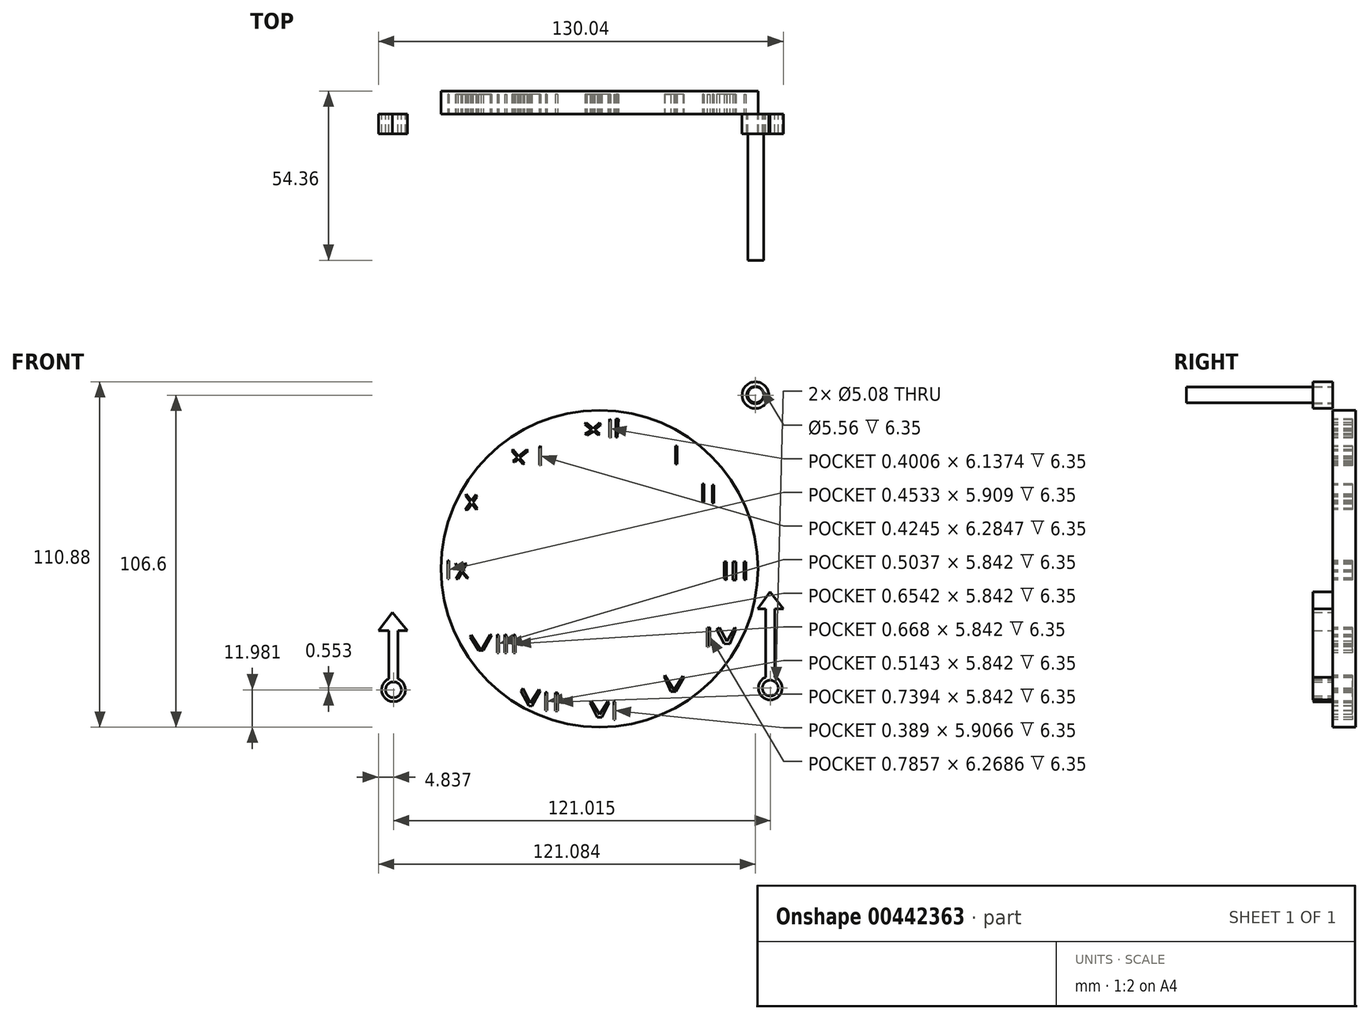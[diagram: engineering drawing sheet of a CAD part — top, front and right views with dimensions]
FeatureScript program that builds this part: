
annotation { "Feature Type Name" : "Feature", "Feature Type Description" : "" }
export const myFeature = defineFeature(function(context is Context, id is Id, definition is map)
    precondition{}
    {
        {
            var Q0;
            Q0=qCreatedBy(makeId("Front.planeOp"),FACE);
            var sketch = newSketch(context, id + "F0", { "sketchPlane" : qUnion([Q0])});
            skLineSegment(sketch, "E0", {"start": v(5.2, 48.06) * mm, "end": v(5.2, 42.22) * mm});
            skLineSegment(sketch, "E1", {"start": v(24.33, 39.4) * mm, "end": v(24.33, 33.55) * mm});
            skLineSegment(sketch, "E2", {"start": v(33.55, 27.23) * mm, "end": v(33.55, 21.39) * mm});
            skLineSegment(sketch, "E3", {"start": v(36.69, 26.86) * mm, "end": v(36.69, 21.02) * mm});
            skLineSegment(sketch, "E4", {"start": v(47.01, 2.15) * mm, "end": v(47.01, -3.69) * mm});
            skLineSegment(sketch, "E5", {"start": v(43.88, 2.15) * mm, "end": v(43.88, -3.69) * mm});
            skLineSegment(sketch, "E6", {"start": v(40.74, 2.15) * mm, "end": v(40.74, -3.69) * mm});
            skLineSegment(sketch, "E7", {"start": v(3.18, 42.22) * mm, "end": v(3.18, 48.06) * mm});
            skLineSegment(sketch, "E8", {"start": v(35.4, -18.86) * mm, "end": v(35.4, -24.7) * mm});
            skLineSegment(sketch, "E9", {"start": v(4.6, -42.58) * mm, "end": v(4.6, -48.42) * mm});
            skLineSegment(sketch, "E10", {"start": v(-14.24, -45.7) * mm, "end": v(-14.24, -39.86) * mm});
            skLineSegment(sketch, "E11", {"start": v(-17.34, -45.55) * mm, "end": v(-17.34, -39.7) * mm});
            skLineSegment(sketch, "E12", {"start": v(-41.21, -21.36) * mm, "end": v(-38.04, -26.27) * mm});
            skLineSegment(sketch, "E13", {"start": v(-38.04, -26.27) * mm, "end": v(-35.16, -21.18) * mm});
            skLineSegment(sketch, "E14", {"start": v(-32.84, -21.18) * mm, "end": v(-32.84, -27.02) * mm});
            skLineSegment(sketch, "E15", {"start": v(-30.51, -21.18) * mm, "end": v(-30.51, -27.02) * mm});
            skLineSegment(sketch, "E16", {"start": v(-27.72, -21.18) * mm, "end": v(-27.72, -27.02) * mm});
            skLineSegment(sketch, "E17", {"start": v(-48.34, 2.62) * mm, "end": v(-48.34, -3.23) * mm});
            skLineSegment(sketch, "E18", {"start": v(-46.02, -3.23) * mm, "end": v(-44.58, -0.7) * mm});
            skLineSegment(sketch, "E19", {"start": v(-46.33, 1.42) * mm, "end": v(-44.58, -0.7) * mm});
            skLineSegment(sketch, "E20", {"start": v(-42.77, 23.97) * mm, "end": v(-41.14, 21.84) * mm});
            skLineSegment(sketch, "E21", {"start": v(-39.79, 23.77) * mm, "end": v(-41.14, 21.84) * mm});
            skLineSegment(sketch, "E22", {"start": v(-27.84, 38.3) * mm, "end": v(-26.03, 36.09) * mm});
            skLineSegment(sketch, "E23", {"start": v(-23.3, 38.3) * mm, "end": v(-26.03, 36.09) * mm});
            skLineSegment(sketch, "E24", {"start": v(-19.28, 39.15) * mm, "end": v(-19.28, 33.3) * mm});
            skCircle(sketch, "E25", {"center": v(0, 0) * mm, "radius": 3.18 * mm});
            skCircle(sketch, "E26", {"center": v(-66.18, -38.9) * mm, "radius": 3.81 * mm});
            skLineSegment(sketch, "E27", {"start": v(-64.7, -38.9) * mm, "end": v(-64.7, -19.85) * mm});
            skLineSegment(sketch, "E28", {"start": v(-67.67, -38.9) * mm, "end": v(-67.67, -19.85) * mm});
            skLineSegment(sketch, "E29", {"start": v(-71.02, -19.85) * mm, "end": v(-61.76, -19.85) * mm});
            skLineSegment(sketch, "E30", {"start": v(-71.02, -19.85) * mm, "end": v(-66.48, -14.05) * mm});
            skLineSegment(sketch, "E31", {"start": v(-61.76, -19.85) * mm, "end": v(-66.48, -14.05) * mm});
            skCircle(sketch, "E32", {"center": v(54.83, -38.35) * mm, "radius": 3.81 * mm});
            skLineSegment(sketch, "E33", {"start": v(54.83, -38.35) * mm, "end": v(56.3, -38.35) * mm});
            skLineSegment(sketch, "E34", {"start": v(54.83, -38.35) * mm, "end": v(53.36, -38.35) * mm});
            skLineSegment(sketch, "E35", {"start": v(56.3, -38.35) * mm, "end": v(56.3, -12.95) * mm});
            skLineSegment(sketch, "E36", {"start": v(53.36, -38.35) * mm, "end": v(53.36, -12.95) * mm});
            skLineSegment(sketch, "E37", {"start": v(50.8, -12.95) * mm, "end": v(59.02, -12.95) * mm});
            skLineSegment(sketch, "E38", {"start": v(50.8, -12.95) * mm, "end": v(54.76, -7.43) * mm});
            skLineSegment(sketch, "E39", {"start": v(54.76, -7.43) * mm, "end": v(59.02, -12.95) * mm});
            skCircle(sketch, "E40", {"center": v(-66.18, -38.9) * mm, "radius": 2.54 * mm});
            skCircle(sketch, "E41", {"center": v(54.83, -38.35) * mm, "radius": 2.54 * mm});
            skLineSegment(sketch, "E42", {"start": v(-48.34, 2.62) * mm, "end": v(-48.8, 2.62) * mm});
            skLineSegment(sketch, "E43", {"start": v(-48.8, 2.62) * mm, "end": v(-48.8, -3.3) * mm});
            skLineSegment(sketch, "E44", {"start": v(-48.8, -3.3) * mm, "end": v(-48.34, -3.23) * mm});
            skLineSegment(sketch, "E45", {"start": v(-46.33, 1.42) * mm, "end": v(-46.18, 1.7) * mm});
            skLineSegment(sketch, "E46", {"start": v(-46.18, 1.7) * mm, "end": v(-44.42, -0.42) * mm});
            skLineSegment(sketch, "E47", {"start": v(-42.22, -3.07) * mm, "end": v(-42.6, -3.07) * mm});
            skLineSegment(sketch, "E48", {"start": v(-43.13, 1.85) * mm, "end": v(-42.78, 1.42) * mm});
            skLineSegment(sketch, "E49", {"start": v(-42.78, 1.42) * mm, "end": v(-44.07, -0.84) * mm});
            skLineSegment(sketch, "E50", {"start": v(-45.43, -3.23) * mm, "end": v(-46.02, -3.23) * mm});
            skLineSegment(sketch, "E51", {"start": v(24.33, 39.4) * mm, "end": v(24.87, 39.4) * mm});
            skLineSegment(sketch, "E52", {"start": v(24.87, 39.4) * mm, "end": v(24.87, 33.55) * mm});
            skLineSegment(sketch, "E53", {"start": v(24.87, 33.55) * mm, "end": v(24.33, 33.55) * mm});
            skLineSegment(sketch, "E54", {"start": v(33.55, 27.23) * mm, "end": v(33.02, 27.23) * mm});
            skLineSegment(sketch, "E55", {"start": v(33.02, 27.23) * mm, "end": v(33.02, 21.42) * mm});
            skLineSegment(sketch, "E56", {"start": v(33.02, 21.42) * mm, "end": v(33.55, 21.39) * mm});
            skLineSegment(sketch, "E57", {"start": v(36.69, 26.86) * mm, "end": v(36.17, 26.86) * mm});
            skLineSegment(sketch, "E58", {"start": v(36.17, 26.86) * mm, "end": v(36.17, 21.16) * mm});
            skLineSegment(sketch, "E59", {"start": v(36.17, 21.16) * mm, "end": v(36.69, 21.02) * mm});
            skLineSegment(sketch, "E60", {"start": v(40.74, -3.69) * mm, "end": v(40.07, -3.3) * mm});
            skLineSegment(sketch, "E61", {"start": v(40.07, -3.3) * mm, "end": v(40.07, 2.15) * mm});
            skLineSegment(sketch, "E62", {"start": v(40.07, 2.15) * mm, "end": v(40.74, 2.15) * mm});
            skLineSegment(sketch, "E63", {"start": v(43.88, -3.69) * mm, "end": v(42.75, -3.69) * mm});
            skLineSegment(sketch, "E64", {"start": v(42.75, -3.69) * mm, "end": v(42.75, 2.15) * mm});
            skLineSegment(sketch, "E65", {"start": v(42.75, 2.15) * mm, "end": v(43.88, 2.15) * mm});
            skLineSegment(sketch, "E66", {"start": v(47.01, -3.69) * mm, "end": v(46.34, -3.3) * mm});
            skLineSegment(sketch, "E67", {"start": v(46.34, -3.3) * mm, "end": v(46.34, 2.15) * mm});
            skLineSegment(sketch, "E68", {"start": v(46.34, 2.15) * mm, "end": v(47.01, 2.15) * mm});
            skLineSegment(sketch, "E69", {"start": v(35.4, -24.7) * mm, "end": v(34.61, -25.13) * mm});
            skLineSegment(sketch, "E70", {"start": v(34.61, -25.13) * mm, "end": v(34.61, -19) * mm});
            skLineSegment(sketch, "E71", {"start": v(34.61, -19) * mm, "end": v(35.4, -18.86) * mm});
            skLineSegment(sketch, "E72", {"start": v(38.49, -18.86) * mm, "end": v(37.65, -19.56) * mm});
            skLineSegment(sketch, "E73", {"start": v(43.45, -18.86) * mm, "end": v(43.88, -19.37) * mm});
            skLineSegment(sketch, "E74", {"start": v(21.02, -34.3) * mm, "end": v(20.8, -34.77) * mm});
            skLineSegment(sketch, "E75", {"start": v(26.83, -34.56) * mm, "end": v(27.06, -35.02) * mm});
            skLineSegment(sketch, "E76", {"start": v(27.06, -35.02) * mm, "end": v(24.49, -39.52) * mm});
            skLineSegment(sketch, "E77", {"start": v(4.6, -42.58) * mm, "end": v(5, -42.76) * mm});
            skLineSegment(sketch, "E78", {"start": v(5, -42.76) * mm, "end": v(5, -48.48) * mm});
            skLineSegment(sketch, "E79", {"start": v(5, -48.48) * mm, "end": v(4.6, -48.42) * mm});
            skLineSegment(sketch, "E80", {"start": v(2.72, -42.58) * mm, "end": v(3, -43.1) * mm});
            skLineSegment(sketch, "E81", {"start": v(3, -43.1) * mm, "end": v(0.82, -47.75) * mm});
            skLineSegment(sketch, "E82", {"start": v(-2.66, -42.55) * mm, "end": v(-3.06, -43.17) * mm});
            skLineSegment(sketch, "E83", {"start": v(-3.06, -43.17) * mm, "end": v(-0.72, -47.75) * mm});
            skLineSegment(sketch, "E84", {"start": v(20.8, -34.77) * mm, "end": v(22.9, -39.43) * mm});
            skLineSegment(sketch, "E85", {"start": v(43.88, -19.37) * mm, "end": v(41.8, -24.25) * mm});
            skLineSegment(sketch, "E86", {"start": v(-19.36, -38.88) * mm, "end": v(-19.04, -39.3) * mm});
            skLineSegment(sketch, "E87", {"start": v(-19.04, -39.3) * mm, "end": v(-21.66, -44.12) * mm});
            skLineSegment(sketch, "E88", {"start": v(-24.67, -38.4) * mm, "end": v(-25.2, -39.38) * mm});
            skLineSegment(sketch, "E89", {"start": v(-25.2, -39.38) * mm, "end": v(-22.68, -44.03) * mm});
            skLineSegment(sketch, "E90", {"start": v(-17.34, -39.7) * mm, "end": v(-16.82, -39.7) * mm});
            skLineSegment(sketch, "E91", {"start": v(-16.82, -39.7) * mm, "end": v(-16.82, -45.5) * mm});
            skLineSegment(sketch, "E92", {"start": v(-16.82, -45.5) * mm, "end": v(-17.34, -45.55) * mm});
            skLineSegment(sketch, "E93", {"start": v(-14.24, -39.86) * mm, "end": v(-13.5, -39.86) * mm});
            skLineSegment(sketch, "E94", {"start": v(-13.5, -39.86) * mm, "end": v(-13.5, -45.7) * mm});
            skLineSegment(sketch, "E95", {"start": v(-13.5, -45.7) * mm, "end": v(-14.24, -45.7) * mm});
            skLineSegment(sketch, "E96", {"start": v(-35.16, -21.18) * mm, "end": v(-34.69, -21.44) * mm});
            skLineSegment(sketch, "E97", {"start": v(-34.69, -21.44) * mm, "end": v(-37.31, -26.28) * mm});
            skLineSegment(sketch, "E98", {"start": v(-41.21, -21.36) * mm, "end": v(-41.53, -21.94) * mm});
            skLineSegment(sketch, "E99", {"start": v(-41.53, -21.94) * mm, "end": v(-38.87, -26.27) * mm});
            skLineSegment(sketch, "E100", {"start": v(-32.84, -21.18) * mm, "end": v(-32.34, -21.46) * mm});
            skLineSegment(sketch, "E101", {"start": v(-32.34, -21.46) * mm, "end": v(-32.34, -27.02) * mm});
            skLineSegment(sketch, "E102", {"start": v(-32.34, -27.02) * mm, "end": v(-32.84, -27.02) * mm});
            skLineSegment(sketch, "E103", {"start": v(-30.51, -21.18) * mm, "end": v(-29.86, -21.54) * mm});
            skLineSegment(sketch, "E104", {"start": v(-29.86, -21.54) * mm, "end": v(-29.86, -27.02) * mm});
            skLineSegment(sketch, "E105", {"start": v(-29.86, -27.02) * mm, "end": v(-30.51, -27.02) * mm});
            skLineSegment(sketch, "E106", {"start": v(-27.72, -21.18) * mm, "end": v(-27.06, -21.55) * mm});
            skLineSegment(sketch, "E107", {"start": v(-27.06, -21.55) * mm, "end": v(-27.06, -27.02) * mm});
            skLineSegment(sketch, "E108", {"start": v(-27.06, -27.02) * mm, "end": v(-27.72, -27.02) * mm});
            skLineSegment(sketch, "E109", {"start": v(-42.77, 23.97) * mm, "end": v(-43.07, 23.4) * mm});
            skLineSegment(sketch, "E110", {"start": v(-43.07, 23.4) * mm, "end": v(-41.5, 21.34) * mm});
            skLineSegment(sketch, "E111", {"start": v(-39.65, 18.94) * mm, "end": v(-39.22, 19.33) * mm});
            skLineSegment(sketch, "E112", {"start": v(-39.79, 23.77) * mm, "end": v(-39.4, 23.07) * mm});
            skLineSegment(sketch, "E113", {"start": v(-39.4, 23.07) * mm, "end": v(-40.69, 21.24) * mm});
            skLineSegment(sketch, "E114", {"start": v(-42.3, 18.92) * mm, "end": v(-43.14, 18.99) * mm});
            skLineSegment(sketch, "E115", {"start": v(-27.84, 38.3) * mm, "end": v(-28.16, 37.71) * mm});
            skLineSegment(sketch, "E116", {"start": v(-28.16, 37.71) * mm, "end": v(-26.47, 35.74) * mm});
            skLineSegment(sketch, "E117", {"start": v(-24.62, 33.58) * mm, "end": v(-24.15, 33.77) * mm});
            skLineSegment(sketch, "E118", {"start": v(-23.3, 38.3) * mm, "end": v(-23.03, 37.8) * mm});
            skLineSegment(sketch, "E119", {"start": v(-23.03, 37.8) * mm, "end": v(-25.63, 35.59) * mm});
            skLineSegment(sketch, "E120", {"start": v(-27.22, 34.22) * mm, "end": v(-27.84, 34.62) * mm});
            skLineSegment(sketch, "E121", {"start": v(-19.28, 39.15) * mm, "end": v(-18.85, 39.38) * mm});
            skLineSegment(sketch, "E122", {"start": v(-18.85, 39.38) * mm, "end": v(-18.85, 33.1) * mm});
            skLineSegment(sketch, "E123", {"start": v(-18.85, 33.1) * mm, "end": v(-19.28, 33.3) * mm});
            skLineSegment(sketch, "E124", {"start": v(-4.35, 46.85) * mm, "end": v(-4.64, 46.31) * mm});
            skLineSegment(sketch, "E125", {"start": v(-0.37, 42.83) * mm, "end": v(0, 43.3) * mm});
            skLineSegment(sketch, "E126", {"start": v(0, 46.85) * mm, "end": v(0.42, 46.07) * mm});
            skLineSegment(sketch, "E127", {"start": v(-4.09, 42.83) * mm, "end": v(-4.64, 43.3) * mm});
            skLineSegment(sketch, "E128", {"start": v(3.17, 48.06) * mm, "end": v(3.58, 47.84) * mm});
            skLineSegment(sketch, "E129", {"start": v(3.58, 47.84) * mm, "end": v(3.58, 41.92) * mm});
            skLineSegment(sketch, "E130", {"start": v(3.58, 41.92) * mm, "end": v(3.18, 42.22) * mm});
            skLineSegment(sketch, "E131", {"start": v(5.2, 48.06) * mm, "end": v(6.05, 48.06) * mm});
            skLineSegment(sketch, "E132", {"start": v(6.05, 48.06) * mm, "end": v(5.7, 42.22) * mm});
            skLineSegment(sketch, "E133", {"start": v(5.7, 42.22) * mm, "end": v(5.2, 42.22) * mm});
            skLineSegment(sketch, "E134", {"start": v(39.99, -24.11) * mm, "end": v(37.65, -19.56) * mm});
            skLineSegment(sketch, "E135", {"start": v(0.42, 46.07) * mm, "end": v(-1.45, 44.56) * mm});
            skLineSegment(sketch, "E136", {"start": v(-1.45, 44.56) * mm, "end": v(0, 43.3) * mm});
            skLineSegment(sketch, "E137", {"start": v(-0.37, 42.83) * mm, "end": v(-1.95, 44.07) * mm});
            skLineSegment(sketch, "E138", {"start": v(-1.95, 44.07) * mm, "end": v(-4.09, 42.83) * mm});
            skLineSegment(sketch, "E139", {"start": v(-4.64, 43.3) * mm, "end": v(-2.48, 44.55) * mm});
            skLineSegment(sketch, "E140", {"start": v(-2.48, 44.55) * mm, "end": v(-4.64, 46.31) * mm});
            skLineSegment(sketch, "E141", {"start": v(-4.35, 46.85) * mm, "end": v(-2.02, 44.93) * mm});
            skLineSegment(sketch, "E142", {"start": v(-2.02, 44.93) * mm, "end": v(0, 46.85) * mm});
            skLineSegment(sketch, "E143.trimOffspring", {"start": v(-25.63, 35.59) * mm, "end": v(-24.15, 33.77) * mm});
            skLineSegment(sketch, "E144.trimOffspring", {"start": v(-26.47, 35.74) * mm, "end": v(-27.84, 34.62) * mm});
            skLineSegment(sketch, "E145.trimOffspring", {"start": v(-26.03, 35.23) * mm, "end": v(-24.62, 33.58) * mm});
            skLineSegment(sketch, "E146.trimOffspring", {"start": v(-26.03, 35.23) * mm, "end": v(-27.22, 34.22) * mm});
            skLineSegment(sketch, "E147.trimOffspring", {"start": v(-41.5, 21.34) * mm, "end": v(-43.14, 18.99) * mm});
            skLineSegment(sketch, "E148.trimOffspring", {"start": v(-41.03, 20.74) * mm, "end": v(-39.65, 18.94) * mm});
            skLineSegment(sketch, "E149.trimOffspring", {"start": v(-41.03, 20.74) * mm, "end": v(-42.3, 18.92) * mm});
            skLineSegment(sketch, "E150.trimOffspring", {"start": v(-40.69, 21.24) * mm, "end": v(-39.22, 19.33) * mm});
            skLineSegment(sketch, "E151", {"start": v(41.8, -24.25) * mm, "end": v(39.99, -24.11) * mm});
            skLineSegment(sketch, "E152", {"start": v(24.49, -39.52) * mm, "end": v(22.9, -39.43) * mm});
            skLineSegment(sketch, "E153", {"start": v(0.82, -47.75) * mm, "end": v(-0.72, -47.75) * mm});
            skLineSegment(sketch, "E154", {"start": v(-19.36, -38.88) * mm, "end": v(-22.16, -43.08) * mm});
            skLineSegment(sketch, "E155", {"start": v(-37.31, -26.28) * mm, "end": v(-38.87, -26.27) * mm});
            skLineSegment(sketch, "E156.trimOffspring", {"start": v(-44.23, -1.12) * mm, "end": v(-45.43, -3.23) * mm});
            skLineSegment(sketch, "E157.trimOffspring", {"start": v(-44.23, -1.12) * mm, "end": v(-42.6, -3.07) * mm});
            skLineSegment(sketch, "E158.trimOffspring", {"start": v(-44.42, -0.42) * mm, "end": v(-43.13, 1.85) * mm});
            skLineSegment(sketch, "E159.trimOffspring", {"start": v(-44.07, -0.84) * mm, "end": v(-42.22, -3.07) * mm});
            skLineSegment(sketch, "E160", {"start": v(-21.66, -44.12) * mm, "end": v(-22.68, -44.03) * mm});
            skLineSegment(sketch, "E161", {"start": v(-24.67, -38.4) * mm, "end": v(-22.16, -43.08) * mm});
            skLineSegment(sketch, "E162", {"start": v(26.83, -34.56) * mm, "end": v(23.9, -38.98) * mm});
            skLineSegment(sketch, "E163", {"start": v(23.9, -38.98) * mm, "end": v(21.02, -34.3) * mm});
            skLineSegment(sketch, "E164", {"start": v(2.72, -42.58) * mm, "end": v(0, -46.85) * mm});
            skLineSegment(sketch, "E165", {"start": v(0, -46.85) * mm, "end": v(-2.66, -42.55) * mm});
            skLineSegment(sketch, "E166", {"start": v(43.45, -18.86) * mm, "end": v(40.91, -23.33) * mm});
            skLineSegment(sketch, "E167", {"start": v(40.91, -23.33) * mm, "end": v(38.49, -18.86) * mm});
            skSolve(sketch);
        }
        {
            var Q0;
            {var subQ0=sQuery(id+"F0.wireOp",EDGE,"E30");Q0=makeQuery(id+"F0.imprint","IMPRINT",FACE,{"disambiguationData":[TD([[makeQuery(id+"F0.imprint","IMPRINT",EDGE,{"derivedFrom":subQ0}),-1.0]])]});}
            var Q1;
            {var subQ0=sQuery(id+"F0.wireOp",EDGE,"E27");var subQ1=sQuery(id+"F0.wireOp",EDGE,"E26");var subQ2=makeQuery(id+"F0.imprint","INTERSECT",VERTEX,{"derivedFrom":[subQ1,subQ0]});Q1=makeQuery(id+"F0.imprint","IMPRINT",FACE,{"disambiguationData":[TD([[makeQuery(id+"F0.imprint","IMPRINT",EDGE,{"disambiguationData":[TD([[subQ2,-1.0]])],"derivedFrom":subQ1}),-1.0]])]});}
            var Q2;
            {var subQ0=sQuery(id+"F0.wireOp",EDGE,"E27");var subQ1=sQuery(id+"F0.wireOp",EDGE,"E26");var subQ2=makeQuery(id+"F0.imprint","INTERSECT",VERTEX,{"derivedFrom":[subQ1,subQ0]});Q2=makeQuery(id+"F0.imprint","IMPRINT",FACE,{"disambiguationData":[TD([[makeQuery(id+"F0.imprint","IMPRINT",EDGE,{"disambiguationData":[TD([[subQ2,1.0]])],"derivedFrom":subQ1}),1.0]])]});}
            var Q3;
            {var subQ0=sQuery(id+"F0.wireOp",EDGE,"E27");var subQ1=sQuery(id+"F0.wireOp",EDGE,"E26");var subQ2=makeQuery(id+"F0.imprint","INTERSECT",VERTEX,{"derivedFrom":[subQ1,subQ0]});Q3=makeQuery(id+"F0.imprint","IMPRINT",FACE,{"disambiguationData":[TD([[makeQuery(id+"F0.imprint","IMPRINT",EDGE,{"disambiguationData":[TD([[subQ2,-1.0]])],"derivedFrom":subQ1}),1.0]])]});}
            var Q4;
            {var subQ0=sQuery(id+"F0.wireOp",EDGE,"E38");Q4=makeQuery(id+"F0.imprint","IMPRINT",FACE,{"disambiguationData":[TD([[makeQuery(id+"F0.imprint","IMPRINT",EDGE,{"derivedFrom":subQ0}),-1.0]])]});}
            var Q5;
            {var subQ0=sQuery(id+"F0.wireOp",EDGE,"E35");var subQ1=sQuery(id+"F0.wireOp",EDGE,"E32");var subQ2=makeQuery(id+"F0.imprint","INTERSECT",VERTEX,{"derivedFrom":[subQ1,subQ0]});Q5=makeQuery(id+"F0.imprint","IMPRINT",FACE,{"disambiguationData":[TD([[makeQuery(id+"F0.imprint","IMPRINT",EDGE,{"disambiguationData":[TD([[subQ2,-1.0]])],"derivedFrom":subQ1}),-1.0]])]});}
            var Q6;
            {var subQ0=sQuery(id+"F0.wireOp",EDGE,"E35");var subQ1=sQuery(id+"F0.wireOp",EDGE,"E32");var subQ2=makeQuery(id+"F0.imprint","INTERSECT",VERTEX,{"derivedFrom":[subQ1,subQ0]});Q6=makeQuery(id+"F0.imprint","IMPRINT",FACE,{"disambiguationData":[TD([[makeQuery(id+"F0.imprint","IMPRINT",EDGE,{"disambiguationData":[TD([[subQ2,1.0]])],"derivedFrom":subQ1}),1.0]])]});}
            var Q7;
            {var subQ0=sQuery(id+"F0.wireOp",EDGE,"E35");var subQ1=sQuery(id+"F0.wireOp",EDGE,"E32");var subQ2=makeQuery(id+"F0.imprint","INTERSECT",VERTEX,{"derivedFrom":[subQ1,subQ0]});Q7=makeQuery(id+"F0.imprint","IMPRINT",FACE,{"disambiguationData":[TD([[makeQuery(id+"F0.imprint","IMPRINT",EDGE,{"disambiguationData":[TD([[subQ2,-1.0]])],"derivedFrom":subQ1}),1.0]])]});}
            extrude(context, id + "F1", {"entities" : qUnion([Q0, Q1, Q2, Q3, Q4, Q5, Q6, Q7]), "depth" : 6.35 * mm});
        }
        {
            var Q0;
            Q0=qCreatedBy(makeId("Front.planeOp"),FACE);
            var sketch = newSketch(context, id + "F2", { "sketchPlane" : qUnion([Q0])});
            skCircle(sketch, "E168", {"center": v(0, 0) * mm, "radius": 50.88 * mm});
            skSolve(sketch);
        }
        {
            var Q0;
            Q0=makeQuery(id+"F2.imprint","IMPRINT",FACE,{"disambiguationData":[TD([[makeQuery(id+"F2.imprint","IMPRINT",EDGE,{"derivedFrom":sQuery(id+"F2.wireOp",EDGE,"E168")}),1.0]])]});
            extrude(context, id + "F3", {"entities" : qUnion([Q0]), "oppositeDirection" : true, "depth" : 7.37 * mm});
        }
        {
            var Q0;
            Q0=makeQuery(id+"F0.imprint","IMPRINT",FACE,{"disambiguationData":[TD([[makeQuery(id+"F0.imprint","IMPRINT",EDGE,{"derivedFrom":sQuery(id+"F0.wireOp",EDGE,"E18")}),-1.0]])]});
            var Q1;
            Q1=makeQuery(id+"F0.imprint","IMPRINT",FACE,{"disambiguationData":[TD([[makeQuery(id+"F0.imprint","IMPRINT",EDGE,{"derivedFrom":sQuery(id+"F0.wireOp",EDGE,"E17")}),-1.0]])]});
            var Q2;
            Q2=makeQuery(id+"F0.imprint","IMPRINT",FACE,{"disambiguationData":[TD([[makeQuery(id+"F0.imprint","IMPRINT",EDGE,{"derivedFrom":sQuery(id+"F0.wireOp",EDGE,"E20")}),-1.0]])]});
            var Q3;
            Q3=makeQuery(id+"F0.imprint","IMPRINT",FACE,{"disambiguationData":[TD([[makeQuery(id+"F0.imprint","IMPRINT",EDGE,{"derivedFrom":sQuery(id+"F0.wireOp",EDGE,"E22")}),-1.0]])]});
            var Q4;
            Q4=makeQuery(id+"F0.imprint","IMPRINT",FACE,{"disambiguationData":[TD([[makeQuery(id+"F0.imprint","IMPRINT",EDGE,{"derivedFrom":sQuery(id+"F0.wireOp",EDGE,"E24")}),1.0]])]});
            var Q5;
            Q5=makeQuery(id+"F0.imprint","IMPRINT",FACE,{"disambiguationData":[TD([[makeQuery(id+"F0.imprint","IMPRINT",EDGE,{"derivedFrom":sQuery(id+"F0.wireOp",EDGE,"E12")}),-1.0]])]});
            var Q6;
            Q6=makeQuery(id+"F0.imprint","IMPRINT",FACE,{"disambiguationData":[TD([[makeQuery(id+"F0.imprint","IMPRINT",EDGE,{"derivedFrom":sQuery(id+"F0.wireOp",EDGE,"E14")}),1.0]])]});
            var Q7;
            Q7=makeQuery(id+"F0.imprint","IMPRINT",FACE,{"disambiguationData":[TD([[makeQuery(id+"F0.imprint","IMPRINT",EDGE,{"derivedFrom":sQuery(id+"F0.wireOp",EDGE,"E15")}),1.0]])]});
            var Q8;
            Q8=makeQuery(id+"F0.imprint","IMPRINT",FACE,{"disambiguationData":[TD([[makeQuery(id+"F0.imprint","IMPRINT",EDGE,{"derivedFrom":sQuery(id+"F0.wireOp",EDGE,"E16")}),1.0]])]});
            var Q9;
            Q9=makeQuery(id+"F0.imprint","IMPRINT",FACE,{"disambiguationData":[TD([[makeQuery(id+"F0.imprint","IMPRINT",EDGE,{"derivedFrom":sQuery(id+"F0.wireOp",EDGE,"E86")}),-1.0]])]});
            var Q10;
            Q10=makeQuery(id+"F0.imprint","IMPRINT",FACE,{"disambiguationData":[TD([[makeQuery(id+"F0.imprint","IMPRINT",EDGE,{"derivedFrom":sQuery(id+"F0.wireOp",EDGE,"E11")}),-1.0]])]});
            var Q11;
            Q11=makeQuery(id+"F0.imprint","IMPRINT",FACE,{"disambiguationData":[TD([[makeQuery(id+"F0.imprint","IMPRINT",EDGE,{"derivedFrom":sQuery(id+"F0.wireOp",EDGE,"E10")}),-1.0]])]});
            var Q12;
            Q12=makeQuery(id+"F0.imprint","IMPRINT",FACE,{"disambiguationData":[TD([[makeQuery(id+"F0.imprint","IMPRINT",EDGE,{"derivedFrom":sQuery(id+"F0.wireOp",EDGE,"E80")}),-1.0]])]});
            var Q13;
            Q13=makeQuery(id+"F0.imprint","IMPRINT",FACE,{"disambiguationData":[TD([[makeQuery(id+"F0.imprint","IMPRINT",EDGE,{"derivedFrom":sQuery(id+"F0.wireOp",EDGE,"E9")}),1.0]])]});
            var Q14;
            Q14=makeQuery(id+"F0.imprint","IMPRINT",FACE,{"disambiguationData":[TD([[makeQuery(id+"F0.imprint","IMPRINT",EDGE,{"derivedFrom":sQuery(id+"F0.wireOp",EDGE,"E74")}),1.0]])]});
            var Q15;
            Q15=makeQuery(id+"F0.imprint","IMPRINT",FACE,{"disambiguationData":[TD([[makeQuery(id+"F0.imprint","IMPRINT",EDGE,{"derivedFrom":sQuery(id+"F0.wireOp",EDGE,"E8")}),-1.0]])]});
            var Q16;
            Q16=makeQuery(id+"F0.imprint","IMPRINT",FACE,{"disambiguationData":[TD([[makeQuery(id+"F0.imprint","IMPRINT",EDGE,{"derivedFrom":sQuery(id+"F0.wireOp",EDGE,"E72")}),1.0]])]});
            var Q17;
            Q17=makeQuery(id+"F0.imprint","IMPRINT",FACE,{"disambiguationData":[TD([[makeQuery(id+"F0.imprint","IMPRINT",EDGE,{"derivedFrom":sQuery(id+"F0.wireOp",EDGE,"E6")}),-1.0]])]});
            var Q18;
            Q18=makeQuery(id+"F0.imprint","IMPRINT",FACE,{"disambiguationData":[TD([[makeQuery(id+"F0.imprint","IMPRINT",EDGE,{"derivedFrom":sQuery(id+"F0.wireOp",EDGE,"E5")}),-1.0]])]});
            var Q19;
            Q19=makeQuery(id+"F0.imprint","IMPRINT",FACE,{"disambiguationData":[TD([[makeQuery(id+"F0.imprint","IMPRINT",EDGE,{"derivedFrom":sQuery(id+"F0.wireOp",EDGE,"E4")}),-1.0]])]});
            var Q20;
            Q20=makeQuery(id+"F0.imprint","IMPRINT",FACE,{"disambiguationData":[TD([[makeQuery(id+"F0.imprint","IMPRINT",EDGE,{"derivedFrom":sQuery(id+"F0.wireOp",EDGE,"E1")}),1.0]])]});
            var Q21;
            Q21=makeQuery(id+"F0.imprint","IMPRINT",FACE,{"disambiguationData":[TD([[makeQuery(id+"F0.imprint","IMPRINT",EDGE,{"derivedFrom":sQuery(id+"F0.wireOp",EDGE,"E2")}),-1.0]])]});
            var Q22;
            Q22=makeQuery(id+"F0.imprint","IMPRINT",FACE,{"disambiguationData":[TD([[makeQuery(id+"F0.imprint","IMPRINT",EDGE,{"derivedFrom":sQuery(id+"F0.wireOp",EDGE,"E3")}),-1.0]])]});
            var Q23;
            Q23=makeQuery(id+"F0.imprint","IMPRINT",FACE,{"disambiguationData":[TD([[makeQuery(id+"F0.imprint","IMPRINT",EDGE,{"derivedFrom":sQuery(id+"F0.wireOp",EDGE,"E7")}),-1.0]])]});
            var Q24;
            Q24=makeQuery(id+"F0.imprint","IMPRINT",FACE,{"disambiguationData":[TD([[makeQuery(id+"F0.imprint","IMPRINT",EDGE,{"derivedFrom":sQuery(id+"F0.wireOp",EDGE,"E0")}),1.0]])]});
            var Q25;
            Q25=makeQuery(id+"F0.imprint","IMPRINT",FACE,{"disambiguationData":[TD([[makeQuery(id+"F0.imprint","IMPRINT",EDGE,{"derivedFrom":sQuery(id+"F0.wireOp",EDGE,"E124")}),1.0]])]});
            extrude(context, id + "F4", {"entities" : qUnion([Q0, Q1, Q2, Q3, Q4, Q5, Q6, Q7, Q8, Q9, Q10, Q11, Q12, Q13, Q14, Q15, Q16, Q17, Q18, Q19, Q20, Q21, Q22, Q23, Q24, Q25]), "operationType" : NewBodyOperationType.REMOVE, "oppositeDirection" : true, "depth" : 6.35 * mm});
        }
        {
            var Q0;
            Q0=makeQuery(id+"F0.imprint","IMPRINT",FACE,{"disambiguationData":[TD([[makeQuery(id+"F0.imprint","IMPRINT",EDGE,{"derivedFrom":sQuery(id+"F0.wireOp",EDGE,"E25")}),1.0]])]});
            var sketch = newSketch(context, id + "F5", { "sketchPlane" : qUnion([Q0])});
            skCircle(sketch, "E169", {"center": v(0, 0) * mm, "radius": 3.1 * mm});
            skSolve(sketch);
        }
        {
            var Q0;
            Q0=makeQuery(id+"F0.imprint","IMPRINT",FACE,{"disambiguationData":[TD([[makeQuery(id+"F0.imprint","IMPRINT",EDGE,{"derivedFrom":sQuery(id+"F0.wireOp",EDGE,"E25")}),1.0]])]});
            var Q1;
            Q1=sQuery(id+"F5.wireOp",EDGE,"E169");
            extrude(context, id + "F6", {"entities" : qUnion([Q0]), "operationType" : NewBodyOperationType.REMOVE, "surfaceEntities" : qUnion([Q1]), "depth" : 41.4 * mm});
        }
        {
            var Q0;
            Q0=qCreatedBy(makeId("Front.planeOp"),FACE);
            var sketch = newSketch(context, id + "F7", { "sketchPlane" : qUnion([Q0])});
            skCircle(sketch, "E170", {"center": v(50.14, 55.8) * mm, "radius": 2.54 * mm});
            skSolve(sketch);
        }
        {
            var Q0;
            Q0=makeQuery(id+"F7.imprint","IMPRINT",FACE,{"disambiguationData":[TD([[makeQuery(id+"F7.imprint","IMPRINT",EDGE,{"derivedFrom":sQuery(id+"F7.wireOp",EDGE,"E170")}),1.0]])]});
            var Q1;
            Q1=sQuery(id+"F7.wireOp",EDGE,"E170");
            extrude(context, id + "F8", {"entities" : qUnion([Q0]), "surfaceEntities" : qUnion([Q1]), "depth" : 47 * mm});
        }
        {
            var Q0;
            Q0=qCreatedBy(makeId("Front.planeOp"),FACE);
            var sketch = newSketch(context, id + "F9", { "sketchPlane" : qUnion([Q0])});
            skCircle(sketch, "E171", {"center": v(50.06, 55.72) * mm, "radius": 2.78 * mm});
            skCircle(sketch, "E172", {"center": v(50.06, 55.72) * mm, "radius": 4.28 * mm});
            skSolve(sketch);
        }
        {
            var Q0;
            Q0=makeQuery(id+"F9.imprint","IMPRINT",FACE,{"disambiguationData":[TD([[makeQuery(id+"F9.imprint","IMPRINT",EDGE,{"derivedFrom":sQuery(id+"F9.wireOp",EDGE,"E171")}),-1.0]])]});
            extrude(context, id + "F10", {"entities" : qUnion([Q0]), "depth" : 6.35 * mm});
        }
    });
